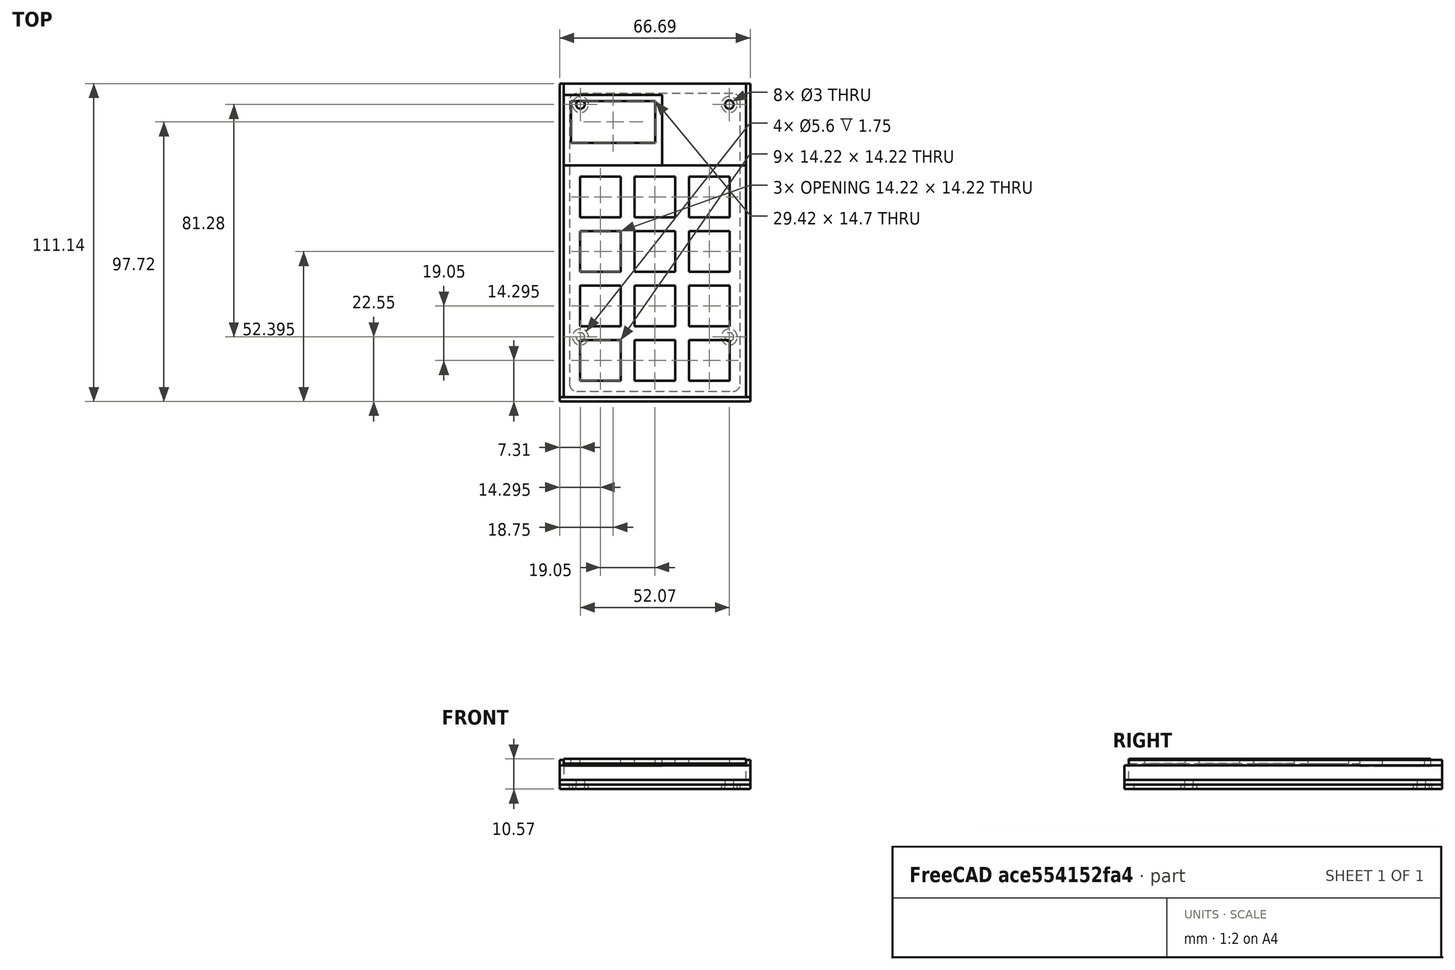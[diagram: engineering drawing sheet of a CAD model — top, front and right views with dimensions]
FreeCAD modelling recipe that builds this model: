
FCSTD DOCUMENT  (FreeCAD 1.0R39109 (Git))
Label: MacroPad-Case
License: All rights reserved
LicenseURL: https://en.wikipedia.org/wiki/All_rights_reserved
objects: Part::Cut×17, Part::Box×15, Part::Cylinder×8, Part::Feature×2, App::DocumentObjectGroup×1
note: 42 computed .brp shape members not serialized (recipe doc carries the construction recipe); baked Part::Feature solids carry a one-line shape summary decoded from their .brp

FEATURE [Part::Feature] Part__Feature  label="Board"
  shape: bbox 59.69 x 104.1 x 1.57 mm, 14 faces (baked)
FEATURE [Part::Box] Box  label="Cube"
  AttacherType = Attacher::AttachEngine3D
  Height = 1.57
  Length = 66.69
  Placement = pos=(-3.5,-3.5,0) rot=(0,0,1;0rad)
  Width = 111.14
FEATURE [Part::Cylinder] Cylinder
  Angle = 360
  AttacherType = Attacher::AttachEngine3D
  FirstAngle = 0
  Height = 10
  Placement = pos=(3.81,19.05,-1) rot=(0,0,1;0rad)
  Radius = 1.5
  SecondAngle = 0
FEATURE [Part::Cylinder] Cylinder001
  Angle = 360
  AttacherType = Attacher::AttachEngine3D
  FirstAngle = 0
  Height = 10
  Placement = pos=(55.88,19.05,-1) rot=(0,0,1;0rad)
  Radius = 1.5
  SecondAngle = 0
FEATURE [Part::Cylinder] Cylinder002
  Angle = 360
  AttacherType = Attacher::AttachEngine3D
  FirstAngle = 0
  Height = 10
  Placement = pos=(3.81,100.33,-1) rot=(0,0,1;0rad)
  Radius = 1.5
  SecondAngle = 0
FEATURE [Part::Cylinder] Cylinder003
  Angle = 360
  AttacherType = Attacher::AttachEngine3D
  FirstAngle = 0
  Height = 10
  Placement = pos=(55.88,100.33,-1) rot=(0,0,1;0rad)
  Radius = 1.5
  SecondAngle = 0
FEATURE [Part::Cylinder] Cylinder004
  Angle = 360
  AttacherType = Attacher::AttachEngine3D
  FirstAngle = 0
  Height = 1.75
  Placement = pos=(3.81,19.05,0) rot=(0,0,1;0rad)
  Radius = 2.8
  SecondAngle = 0
FEATURE [Part::Cylinder] Cylinder005
  Angle = 360
  AttacherType = Attacher::AttachEngine3D
  FirstAngle = 0
  Height = 1.75
  Placement = pos=(55.88,19.05,0) rot=(0,0,1;0rad)
  Radius = 2.8
  SecondAngle = 0
FEATURE [Part::Cylinder] Cylinder006
  Angle = 360
  AttacherType = Attacher::AttachEngine3D
  FirstAngle = 0
  Height = 1.75
  Placement = pos=(3.81,100.33,0) rot=(0,0,1;0rad)
  Radius = 2.8
  SecondAngle = 0
FEATURE [Part::Cylinder] Cylinder007
  Angle = 360
  AttacherType = Attacher::AttachEngine3D
  FirstAngle = 0
  Height = 1.75
  Placement = pos=(55.88,100.33,0) rot=(0,0,1;0rad)
  Radius = 2.8
  SecondAngle = 0
FEATURE [Part::Box] Box001  label="Cube001"
  AttacherType = Attacher::AttachEngine3D
  Height = 3.25
  Length = 66.69
  Placement = pos=(-3.5,-3.5,0) rot=(0,0,1;0rad)
  Width = 111.14
FEATURE [Part::Cut] Cut
  Base = -> Box001
  Tool = -> Cylinder
FEATURE [Part::Cut] Cut001
  Base = -> Cut
  Tool = -> Cylinder001
FEATURE [Part::Cut] Cut002
  Base = -> Cut001
  Tool = -> Cylinder002
FEATURE [Part::Cut] Cut003
  Base = -> Cut002
  Tool = -> Cylinder003
FEATURE [Part::Cut] Cut004
  Base = -> Cut003
  Tool = -> Cylinder004
FEATURE [Part::Cut] Cut005
  Base = -> Cut004
  Tool = -> Cylinder005
FEATURE [Part::Cut] Cut006
  Base = -> Cut005
  Tool = -> Cylinder006
FEATURE [Part::Cut] Cut007
  Base = -> Cut006
  Tool = -> Cylinder007
FEATURE [App::DocumentObjectGroup] Group  label="Posts"
  Group = -> [Cut007]
FEATURE [Part::Box] Box002  label="Cube002"
  AttacherType = Attacher::AttachEngine3D
  Height = 5
  Length = 66.69
  Placement = pos=(-3.5,-3.5,3.25) rot=(0,0,1;0rad)
  Width = 111.14
FEATURE [Part::Box] Box003  label="Cube003"
  AttacherType = Attacher::AttachEngine3D
  Height = 5
  Length = 63.69
  Placement = pos=(-2,-2,3.25) rot=(0,0,1;0rad)
  Width = 108.14
FEATURE [Part::Cut] Cut008
  Base = -> Box002
  Tool = -> Box003
FEATURE [Part::Box] Box005  label="Cube005"
  AttacherType = Attacher::AttachEngine3D
  Height = 5
  Length = 63.69
  Placement = pos=(-2,98,3.25) rot=(0,0,1;0rad)
  Width = 10
FEATURE [Part::Cut] Cut009
  Base = -> Cut008
  Tool = -> Box005
FEATURE [Part::Box] Box008  label="Cube008"
  AttacherType = Attacher::AttachEngine3D
  Height = 1.57
  Length = 63.69
  Placement = pos=(-2,-2,9) rot=(0,0,1;0rad)
  Width = 81
FEATURE [Part::Box] Box010  label="Cube010"
  AttacherType = Attacher::AttachEngine3D
  Height = 2.57
  Length = 34.4
  Placement = pos=(-2,79,8) rot=(0,0,1;0rad)
  Width = 24.73
FEATURE [Part::Box] Box011  label="Cube011"
  AttacherType = Attacher::AttachEngine3D
  Height = 2.57
  Length = 29.42
  Placement = pos=(0.54,86.87,8) rot=(0,0,1;0rad)
  Width = 14.7
FEATURE [Part::Cut] Cut011
  Base = -> Box010
  Tool = -> Box011
FEATURE [Part::Feature] Part__Feature180  label="Board002"
  Placement = pos=(0,0,9) rot=(0,0,1;0rad)
  shape: bbox 59.69 x 78.74 x 1.57 mm, 61 faces (baked)
FEATURE [Part::Box] Box012  label="Cube012"
  AttacherType = Attacher::AttachEngine3D
  Height = 1.57
  Length = 63.69
  Placement = pos=(-2,-2,9) rot=(0,0,1;0rad)
  Width = 81
FEATURE [Part::Cut] Cut012
  Base = -> Box008
  Tool = -> Part__Feature180
FEATURE [Part::Box] Box013  label="Cube013"
  AttacherType = Attacher::AttachEngine3D
  Height = 1.57
  Length = 63.69
  Placement = pos=(-61,-2,9) rot=(0,0,1;0rad)
  Width = 81
FEATURE [Part::Box] Box014  label="Cube014"
  AttacherType = Attacher::AttachEngine3D
  Height = 1.57
  Length = 63.69
  Placement = pos=(-2,76,9) rot=(0,0,1;0rad)
  Width = 81
FEATURE [Part::Cut] Cut013
  Base = -> Cut012
  Tool = -> Box013
FEATURE [Part::Box] Box015  label="Cube015"
  AttacherType = Attacher::AttachEngine3D
  Height = 1.57
  Length = 63.69
  Placement = pos=(57,-3,9) rot=(0,0,1;0rad)
  Width = 81
FEATURE [Part::Cut] Cut014
  Base = -> Cut013
  Tool = -> Box014
FEATURE [Part::Box] Box016  label="Cube016"
  AttacherType = Attacher::AttachEngine3D
  Height = 1.57
  Length = 63.69
  Placement = pos=(-4,-79,9) rot=(0,0,1;0rad)
  Width = 81
FEATURE [Part::Cut] Cut015
  Base = -> Cut014
  Tool = -> Box015
FEATURE [Part::Cut] Cut016
  Base = -> Cut015
  Tool = -> Box016
FEATURE [Part::Cut] Cut017
  Base = -> Box012
  Tool = -> Cut016
FEATURE [Part::Box] Box017  label="Cube017"
  AttacherType = Attacher::AttachEngine3D
  Height = 2
  Length = 1.5
  Placement = pos=(-3.5,-2,8.25) rot=(0,0,1;0rad)
  Width = 109.64
FEATURE [Part::Box] Box018  label="Cube018"
  AttacherType = Attacher::AttachEngine3D
  Height = 2
  Length = 1.5
  Placement = pos=(61.69,-2,8.25) rot=(0,0,1;0rad)
  Width = 109.64
